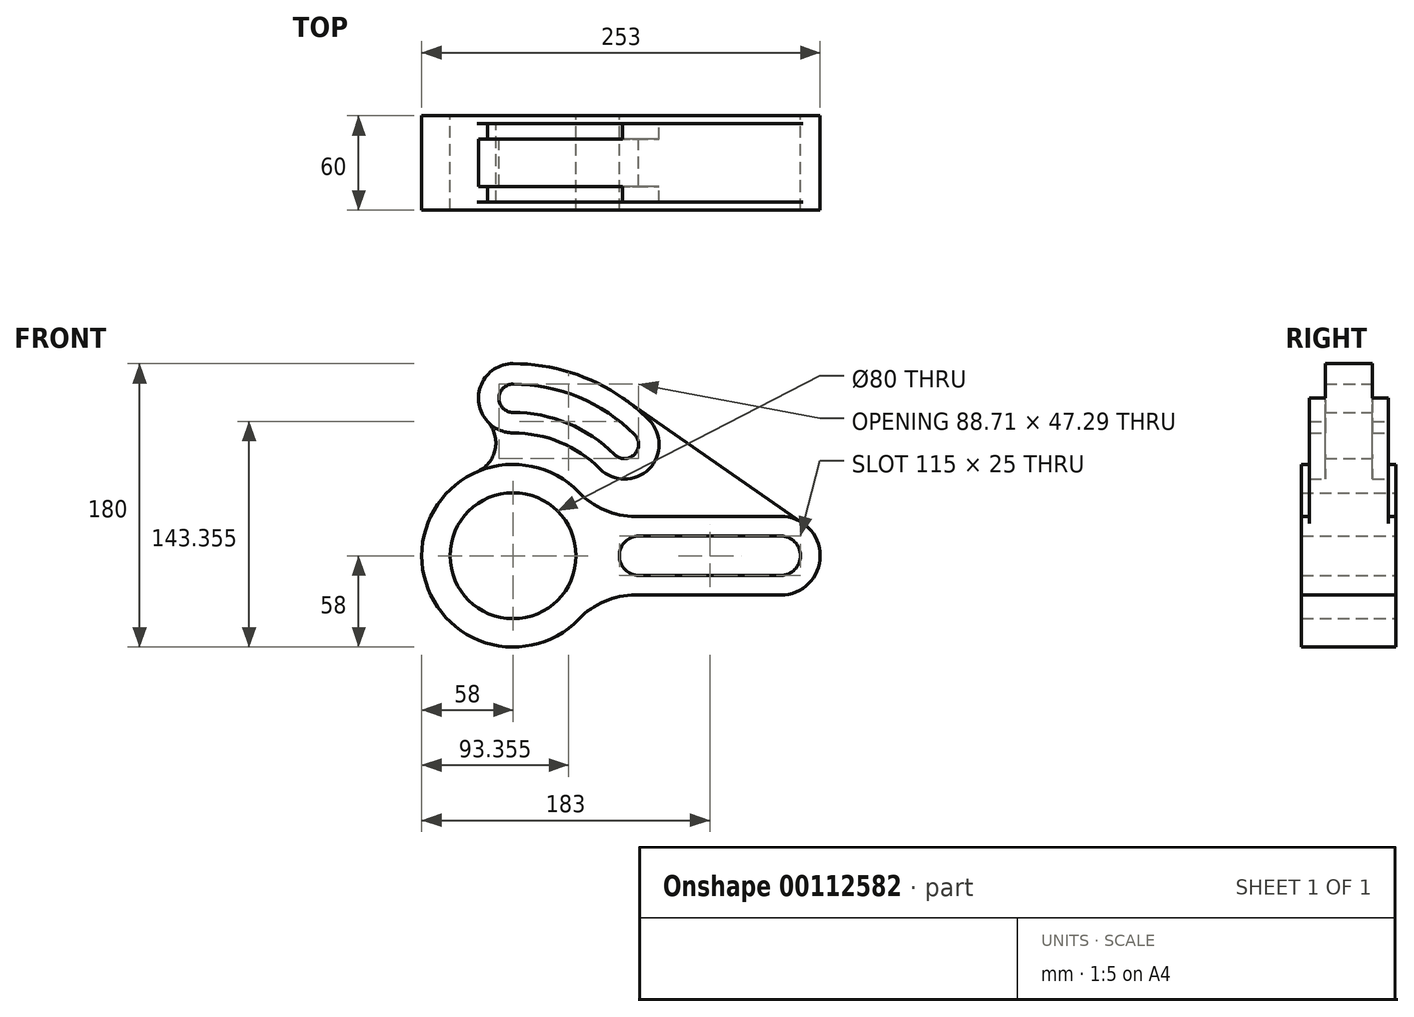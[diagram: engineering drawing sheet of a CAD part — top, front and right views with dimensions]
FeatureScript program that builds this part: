
annotation { "Feature Type Name" : "Feature", "Feature Type Description" : "" }
export const myFeature = defineFeature(function(context is Context, id is Id, definition is map)
    precondition{}
    {
        {
            var Q0;
            Q0=qCreatedBy(makeId("Front.planeOp"),FACE);
            var sketch = newSketch(context, id + "F0", { "sketchPlane" : qUnion([Q0])});
            skCircle(sketch, "E0", {"center": v(0, 0) * mm, "radius": 40 * mm});
            skLineSegment(sketch, "E1", {"start": v(80, 0) * mm, "end": v(170, 0) * mm, "construction": true});
            skArc(sketch, "E2.0.startCap", {"start": v(80, -12.5) * mm, "mid": v(67.5, 0) * mm, "end": v(80, 12.5) * mm});
            skArc(sketch, "E2.0.endCap", {"start": v(170, 12.5) * mm, "mid": v(182.5, 0) * mm, "end": v(170, -12.5) * mm});
            skLineSegment(sketch, "E2.0.left", {"start": v(80, 12.5) * mm, "end": v(170, 12.5) * mm});
            skLineSegment(sketch, "E2.0.right", {"start": v(80, -12.5) * mm, "end": v(170, -12.5) * mm});
            skArc(sketch, "E3", {"start": v(0, 100) * mm, "mid": v(38.27, 92.39) * mm, "end": v(70.71, 70.71) * mm, "construction": true});
            skLineSegment(sketch, "E4", {"start": v(80, 32.17) * mm, "end": v(80, -75.88) * mm, "construction": true});
            skArc(sketch, "E5.0.startCap", {"start": v(0, 78) * mm, "mid": v(-22, 100) * mm, "end": v(0, 122) * mm});
            skArc(sketch, "E5.0.endCap", {"start": v(86.27, 86.27) * mm, "mid": v(86.27, 55.15) * mm, "end": v(55.15, 55.15) * mm});
            skArc(sketch, "E5.0.left", {"start": v(0, 122) * mm, "mid": v(46.69, 112.71) * mm, "end": v(86.27, 86.27) * mm});
            skArc(sketch, "E5.0.right", {"start": v(0, 78) * mm, "mid": v(29.85, 72.06) * mm, "end": v(55.15, 55.15) * mm});
            skArc(sketch, "E6", {"start": v(41.73, 40.28) * mm, "mid": v(-58, 0) * mm, "end": v(41.73, -40.28) * mm});
            skArc(sketch, "E7.0", {"start": v(0, 91) * mm, "mid": v(34.82, 84.07) * mm, "end": v(64.35, 64.35) * mm});
            skArc(sketch, "E7.1", {"start": v(0, 91) * mm, "mid": v(-9, 100) * mm, "end": v(0, 109) * mm});
            skArc(sketch, "E7.2", {"start": v(0, 109) * mm, "mid": v(41.71, 100.7) * mm, "end": v(77.07, 77.07) * mm});
            skArc(sketch, "E7.3", {"start": v(77.07, 77.07) * mm, "mid": v(77.07, 64.35) * mm, "end": v(64.35, 64.35) * mm});
            skLineSegment(sketch, "E8", {"start": v(77.71, -25) * mm, "end": v(170, -25) * mm});
            skLineSegment(sketch, "E9", {"start": v(77.71, 25) * mm, "end": v(170, 25) * mm});
            skArc(sketch, "E10", {"start": v(170, -25) * mm, "mid": v(195, 0) * mm, "end": v(170, 25) * mm});
            skArc(sketch, "E11", {"start": v(-23, 53.24) * mm, "mid": v(-11.38, 67.43) * mm, "end": v(-16.2, 85.12) * mm});
            skLineSegment(sketch, "E12", {"start": v(69.61, 100.2) * mm, "end": v(184.26, 20.53) * mm});
            skPoint(sketch, "E13.visualSharp", {"position": v(52.34, -25) * mm});
            skArc(sketch, "E13.filletArc", {"start": v(77.71, -25) * mm, "mid": v(58.17, -28.98) * mm, "end": v(41.73, -40.28) * mm});
            skPoint(sketch, "E14.visualSharp", {"position": v(52.34, 25) * mm});
            skArc(sketch, "E14.filletArc", {"start": v(41.73, 40.28) * mm, "mid": v(58.17, 28.98) * mm, "end": v(77.71, 25) * mm});
            skLineSegment(sketch, "E15", {"start": v(0, 0) * mm, "end": v(0, 152.57) * mm, "construction": true});
            skLineSegment(sketch, "E16", {"start": v(0, 0) * mm, "end": v(104.14, 104.14) * mm, "construction": true});
            skSolve(sketch);
        }
        {
            var Q0;
            {var subQ2=sQuery(id+"F0.wireOp",EDGE,"E5.0.endCap");Q0=makeQuery(id+"F0.imprint","IMPRINT",FACE,{"disambiguationData":[TD([[makeQuery(id+"F0.imprint","IMPRINT",EDGE,{"derivedFrom":subQ2}),1.0]])]});}
            extrude(context, id + "F1", {"entities" : qUnion([Q0]), "depth" : 30 * mm, "symmetric" : true});
        }
        {
            var Q0;
            Q0=makeQuery(id+"F0.imprint","IMPRINT",FACE,{"disambiguationData":[TD([[makeQuery(id+"F0.imprint","IMPRINT",EDGE,{"derivedFrom":sQuery(id+"F0.wireOp",EDGE,"E0")}),-1.0]])]});
            extrude(context, id + "F2", {"entities" : qUnion([Q0]), "operationType" : NewBodyOperationType.ADD, "depth" : 60 * mm, "symmetric" : true});
        }
        {
            var Q0;
            {var subQ4=sQuery(id+"F0.wireOp",EDGE,"E5.0.endCap");Q0=makeQuery(id+"F0.imprint","IMPRINT",FACE,{"disambiguationData":[TD([[makeQuery(id+"F0.imprint","IMPRINT",EDGE,{"derivedFrom":subQ4}),-1.0]])]});}
            extrude(context, id + "F3", {"entities" : qUnion([Q0]), "operationType" : NewBodyOperationType.ADD, "depth" : 50 * mm, "symmetric" : true});
        }
        {
            var Q0;
            {var subQ4=sQuery(id+"F0.wireOp",EDGE,"E5.0.endCap");Q0=makeQuery(id+"F0.imprint","IMPRINT",FACE,{"disambiguationData":[TD([[makeQuery(id+"F0.imprint","IMPRINT",EDGE,{"derivedFrom":subQ4}),-1.0]])]});}
            extrude(context, id + "F4", {"entities" : qUnion([Q0]), "operationType" : NewBodyOperationType.ADD, "depth" : 50 * mm, "symmetric" : true});
        }
    });
